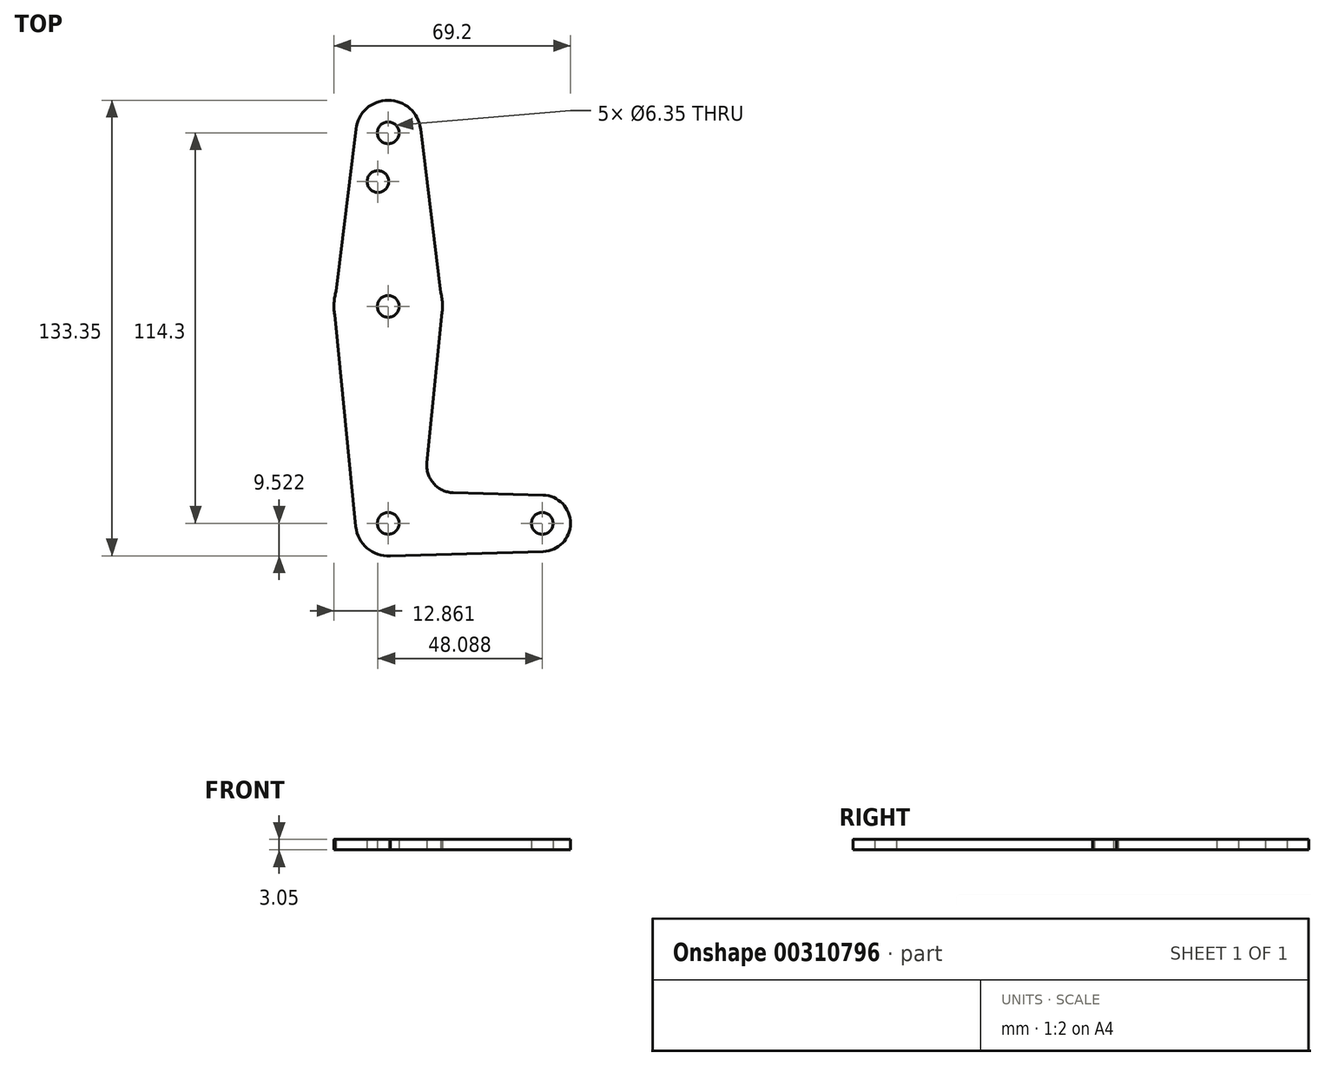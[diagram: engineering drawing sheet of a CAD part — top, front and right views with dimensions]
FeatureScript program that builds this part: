
annotation { "Feature Type Name" : "Feature", "Feature Type Description" : "" }
export const myFeature = defineFeature(function(context is Context, id is Id, definition is map)
    precondition{}
    {
        {
            var Q0;
            Q0=qCreatedBy(makeId("Top.planeOp"),FACE);
            var sketch = newSketch(context, id + "F0", { "sketchPlane" : qUnion([Q0])});
            skCircle(sketch, "E0", {"center": v(-35.16, 13.06) * mm, "radius": 15.88 * mm});
            skCircle(sketch, "E1", {"center": v(-35.16, 63.86) * mm, "radius": 3.18 * mm});
            skCircle(sketch, "E2", {"center": v(-35.16, 63.86) * mm, "radius": 9.53 * mm});
            skCircle(sketch, "E3", {"center": v(-35.16, -50.44) * mm, "radius": 9.53 * mm});
            skCircle(sketch, "E4", {"center": v(-35.16, -50.44) * mm, "radius": 3.18 * mm});
            skCircle(sketch, "E5", {"center": v(9.92, -50.44) * mm, "radius": 8.26 * mm});
            skCircle(sketch, "E6", {"center": v(9.92, -50.44) * mm, "radius": 3.18 * mm});
            skCircle(sketch, "E7", {"center": v(-35.16, 13.06) * mm, "radius": 3.18 * mm});
            skLineSegment(sketch, "E8", {"start": v(-19.28, 12.88) * mm, "end": v(-25.7, 65.03) * mm});
            skLineSegment(sketch, "E9", {"start": v(-51.02, 12.36) * mm, "end": v(-44.61, 65.03) * mm});
            skLineSegment(sketch, "E10", {"start": v(-51.02, 12.36) * mm, "end": v(-44.61, -51.63) * mm});
            skLineSegment(sketch, "E11", {"start": v(-19.28, 12.88) * mm, "end": v(-23.82, -32.73) * mm});
            skLineSegment(sketch, "E12", {"start": v(-16.13, -41.46) * mm, "end": v(10.15, -42.19) * mm});
            skLineSegment(sketch, "E13", {"start": v(-35.2, -59.96) * mm, "end": v(10.15, -58.69) * mm});
            skCircle(sketch, "E14", {"center": v(-38.17, 49.6) * mm, "radius": 3.18 * mm});
            skLineSegment(sketch, "E15.trimOffspring", {"start": v(-19.3, 13) * mm, "end": v(-19.28, 13) * mm, "construction": true});
            skPoint(sketch, "E16.orphan", {"position": v(5.9, 12.88) * mm});
            skPoint(sketch, "E17.newPointA", {"position": v(-25.7, -51.63) * mm});
            skArc(sketch, "E17.filletArc", {"start": v(-23.82, -32.73) * mm, "mid": v(-21.88, -38.77) * mm, "end": v(-16.13, -41.46) * mm});
            skSolve(sketch);
        }
        {
            var Q0;
            Q0 = qSketchRegion(id + "F0", true);
            extrude(context, id + "F1", {"entities" : qUnion([Q0]), "depth" : 3.05 * mm});
        }
    });
